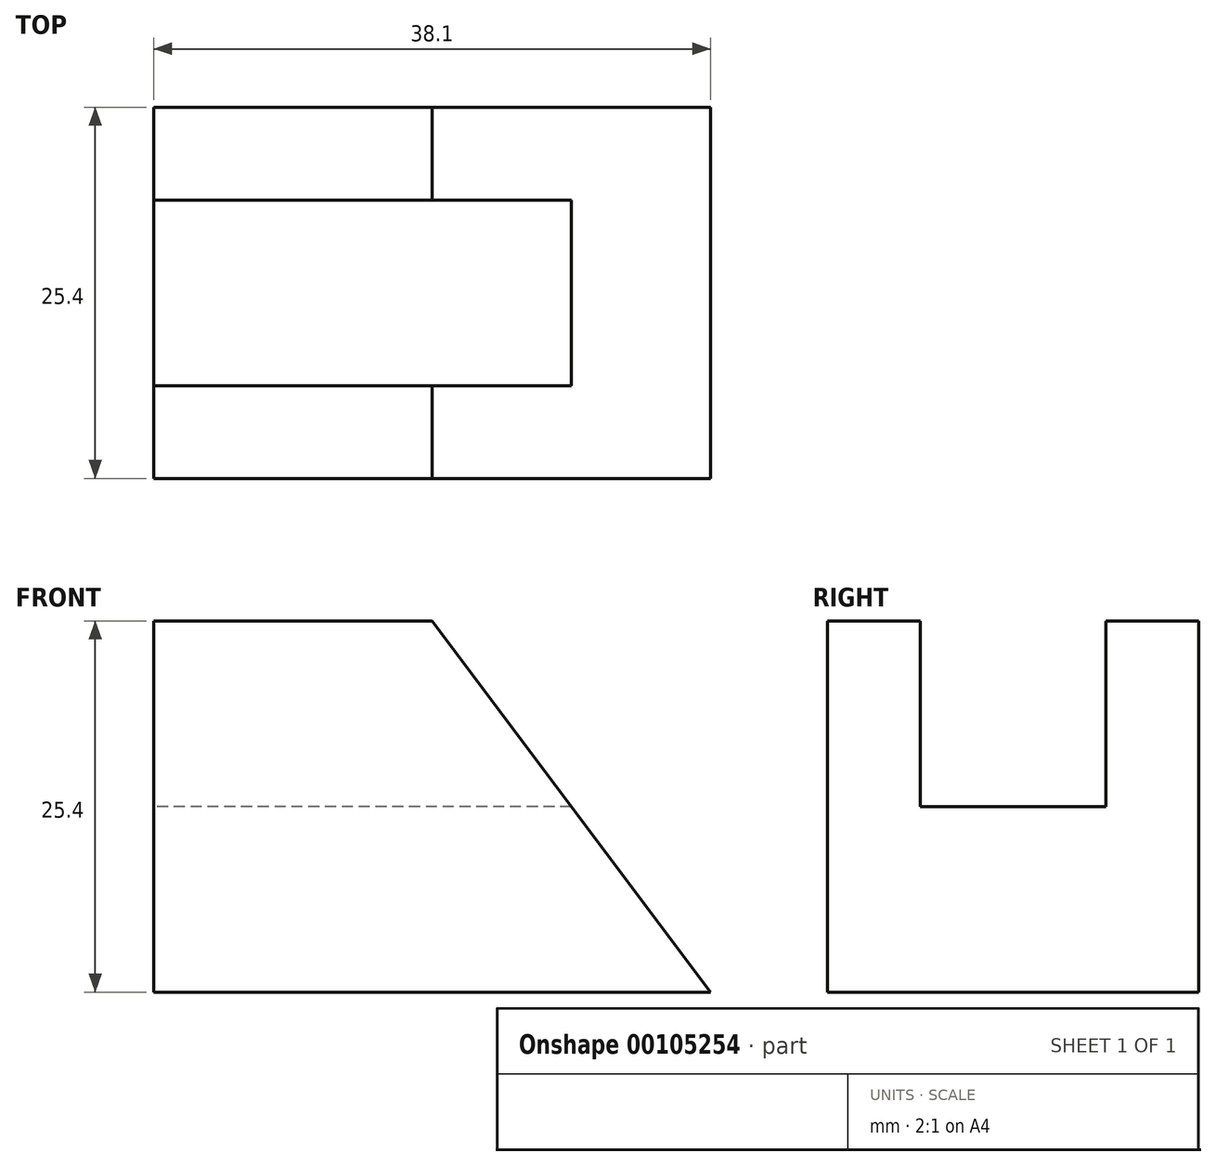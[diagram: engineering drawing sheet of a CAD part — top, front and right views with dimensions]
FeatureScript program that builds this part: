
annotation { "Feature Type Name" : "Feature", "Feature Type Description" : "" }
export const myFeature = defineFeature(function(context is Context, id is Id, definition is map)
    precondition{}
    {
        {
            var Q0;
            Q0=qCreatedBy(makeId("Front.planeOp"),FACE);
            var sketch = newSketch(context, id + "F0", { "sketchPlane" : qUnion([Q0])});
            skLineSegment(sketch, "E0.bottom", {"start": v(0, 0) * mm, "end": v(38.1, 0) * mm});
            skLineSegment(sketch, "E0.top", {"start": v(0, 25.4) * mm, "end": v(38.1, 25.4) * mm});
            skLineSegment(sketch, "E0.left", {"start": v(0, 0) * mm, "end": v(0, 25.4) * mm});
            skLineSegment(sketch, "E0.right", {"start": v(38.1, 0) * mm, "end": v(38.1, 25.4) * mm});
            skSolve(sketch);
        }
        {
            var Q0;
            Q0 = qSketchRegion(id + "F0", true);
            extrude(context, id + "F1", {"entities" : qUnion([Q0]), "endBound" : BoundingType.SYMMETRIC, "depth" : 25.4 * mm});
        }
        {
            var Q0;
            Q0=makeQuery(id+"F1.opExtrude","CAP_FACE",FACE,{"disambiguationData":[OSD([sQuery(id+"F0.wireOp",EDGE,"E0.bottom"),sQuery(id+"F0.wireOp",EDGE,"E0.top"),sQuery(id+"F0.wireOp",EDGE,"E0.left"),sQuery(id+"F0.wireOp",EDGE,"E0.right")])],"isStart":false});
            var sketch = newSketch(context, id + "F2", { "sketchPlane" : qUnion([Q0])});
            skLineSegment(sketch, "E1", {"start": v(38.1, 0) * mm, "end": v(19.05, 25.4) * mm});
            skSolve(sketch);
        }
        {
            var Q0;
            {var subQ0=sQuery(id+"F2.wireOp",EDGE,"E1");Q0=makeQuery(id+"F2.imprint","IMPRINT",FACE,{"disambiguationData":[TD([[makeQuery(id+"F2.imprint","IMPRINT",EDGE,{"derivedFrom":subQ0}),-1.0]])]});}
            extrude(context, id + "F3", {"entities" : qUnion([Q0]), "operationType" : NewBodyOperationType.REMOVE, "endBound" : BoundingType.THROUGH_ALL, "oppositeDirection" : true, "depth" : 25.4 * mm});
        }
        {
            var Q0;
            Q0=makeQuery(id+"F1.opExtrude","SWEPT_FACE",FACE,{"disambiguationData":[OSD([sQuery(id+"F0.wireOp",EDGE,"E0.left")])]});
            var sketch = newSketch(context, id + "F4", { "sketchPlane" : qUnion([Q0])});
            skLineSegment(sketch, "E2.bottom", {"start": v(-6.35, 25.4) * mm, "end": v(6.35, 25.4) * mm});
            skLineSegment(sketch, "E2.top", {"start": v(-6.35, 12.7) * mm, "end": v(6.35, 12.7) * mm});
            skLineSegment(sketch, "E2.left", {"start": v(-6.35, 25.4) * mm, "end": v(-6.35, 12.7) * mm});
            skLineSegment(sketch, "E2.right", {"start": v(6.35, 25.4) * mm, "end": v(6.35, 12.7) * mm});
            skSolve(sketch);
        }
        {
            var Q0;
            Q0=makeQuery(id+"F4.imprint","IMPRINT",FACE,{"disambiguationData":[TD([[makeQuery(id+"F4.imprint","IMPRINT",EDGE,{"derivedFrom":sQuery(id+"F4.wireOp",EDGE,"E2.bottom")}),1.0]])]});
            extrude(context, id + "F5", {"entities" : qUnion([Q0]), "operationType" : NewBodyOperationType.REMOVE, "endBound" : BoundingType.THROUGH_ALL, "oppositeDirection" : true, "depth" : 25.4 * mm});
        }
    });
